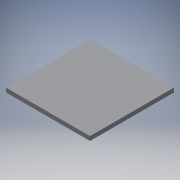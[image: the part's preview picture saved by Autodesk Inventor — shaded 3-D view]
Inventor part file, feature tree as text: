
AUTODESK INVENTOR PART (.ipt)
format: ipt  version: 2018.3 (Build 223284000, 284)  size: 82,432 bytes
history: native  units: mm
features: extrude x1, sketch x1
ambient origin geometry x8: Origin, YZ Plane, XZ Plane, XY Plane, X Axis, Y Axis, Z Axis, Center Point
bodies: Solid1 (feature_tree)
feature tree (2):
  extrude  "Extrusion1"  Depth=40.0mm
  sketch  "Sketch1"  dims[d0=40.0mm d1=40.0mm d2=2.0mm d3=0.0mm]
